# Revit family: Maxlogic Неадресный ПКП большой корпус
name_source: partatom
category: Fire Alarm Devices
units: mm (PartAtom-declared; Revit-internal decimal feet)

## family parameters
Cut with Voids When Loaded = No
Host = Face
Maintain Annotation Orientation = Yes
OmniClass Number = 23.85.30.21
OmniClass Title = Environmental Detection/Registration
Part Type = Normal
Room Calculation Point = No
Round Connector Dimension = Use Diameter
Shared = No

## types (4) — shared parameters
Manufacturer = Mavili Elektronik Ticaret A.Ş.
Model = Maxlogic
URL = https://www.mavili.com.tr
Адрес №1 = Şerifali Mahallesi Kutup Sokak No:27/1-2-4 Ümraniye TR-34775 İSTANBUL
Гарантийный срок = Года
Гарантийный срок запчастей = 2
Гарантия срока службы = 2
Главный Материал = Серый металлический
Инструкция по установке = https://mavilielektronik.com
Монтажная поверхность = Настенная
Номер телефона = (+)90 216 466 45 05
Номер факса = (+)90 216 466 45 10
Номинальная высота = 300 мм
Номинальная глубина = 100 мм
Номинальная ширина = 400 мм
Производительность кода = EN 54-2 / EN 54-4
Рабочая Температура = (-5°C) - (+50°C)
Резервное питание = 220 В Перем. ток
Цвет = Белый
zero-valued in all types: Cost, Default Elevation

## per-type parameters (varying)
| type | Description | Аккумулятор | Вес | Вторичный материал | Код продукта | Номер позы общественных работ | привело 2 | привело 4 | привело 8 |
| Maxlogic Неадресный пожарный приемно-контрольный прибор, 16 шлейфов | Неадресный пожарный приемно-контрольный прибор, 16 шлейфов | 2 X  (12В Пост. ток 7 Aм/ч. ) | ~ 4,275 - 4,4 кг (без аккумулятора) | Белый пластмассовый ABS | ML-22116 | 833-214 | Yes | Yes | Yes |
| Maxlogic Неадресный пожарный приемно-контрольный прибор, 8 шлейфов | Неадресный пожарный приемно-контрольный прибор, 8 шлейфов | 2 X  (12В Пост. ток 7 Aм/ч. ) | ~ 4,275 - 4,4 кг (без аккумулятора) | Белый пластмассовый ABS | ML-22108 | 833-212 | Yes | Yes | No |
| Maxlogic Неадресный пожарный приемно-контрольный прибор, 4 шлейфа | Неадресный пожарный приемно-контрольный прибор, 4 шлейфа | 2 X  (12В Пост. ток 7 Aм/ч. ) | ~ 4,275 - 4,4 кг (без аккумулятора) | White Plastic ABS | ML-22104 | 833-211 | Yes | No | No |
| Maxlogic Неадресный пожарный приемно-контрольный прибор, 2 шлейфа | Неадресный пожарный приемно-контрольный прибор, 2 шлейфа | 2 X (12В Пост. ток 7 Aм/ч. ) | ~ 4,275 - 4,4 kg (без аккумулятора) | Белый пластмассовый ABS | ML-22102 |  | No | No | No |

## geometry (parser evidence)
native form markers: Sweep x1
no freeform markers — native parametric forms only
